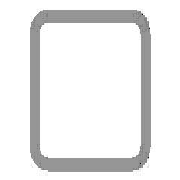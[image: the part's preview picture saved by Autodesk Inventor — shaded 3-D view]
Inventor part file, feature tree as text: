
AUTODESK INVENTOR PART (.ipt)
format: ipt  version: 2025.1 (Build 291241000, 241)  size: 209,920 bytes
history: native  units: mm (DEFAULTED — no unit token found)
features: other x18, sketch x4, extrude x3, plane x1
ambient origin geometry x8: Origin, YZ Plane, XZ Plane, XY Plane, X Axis, Y Axis, Z Axis, Center Point
bodies: Solid1 (feature_tree)
feature tree (26):
  parser-record x1  (decoder bookkeeping rows leaked as tree rows — omitted from the tree; the rows remain in map.json)
  other  "Driven Length"
  other  "Płaszczyzna początkowa"
  other  "Płaszczyzna końcowa"
  extrude  "Bryła"  TaperAngle=0.0deg  [1 undecoded]
  other  "Płaszczyzna konstrukcyjna4"
  other  "Podział1"
  other  "Płaszczyzna konstrukcyjna5"
  other  "Podział2"
  other  "Płaszczyzna konstrukcyjna6"
  other  "Płaszczyzna konstrukcyjna7"
  other  "Płaszczyzna konstrukcyjna8"
  extrude  "Wyciągnięcie proste2"  Depth=4.0mm
  other  "Utwórz kombinację1"
  other  "Płaszczyzna konstrukcyjna9"
  other  "Płaszczyzna konstrukcyjna10"
  other  "Płaszczyzna konstrukcyjna11"
  extrude  "Wyciągnięcie proste3"  Depth=4.0mm
  other  "Utwórz kombinację2"
  sketch  "Sketch3"  dims[d3=1740.0mm d4=0.0mm]
  plane  "Work Plane3"
  sketch  "Sketch4"  dims[d7=4.0mm d10=40.0mm d11=40.0mm d12=3.2mm d13=-20.0mm d14=1720.0mm d15=20.0mm d16=20.0mm d17=90.0deg d18=1740.0mm d19=0.13mm d20=0.0mm d21=0.13mm d22=0.0mm]
  sketch  "Szkic5"
  other  "Bryła2"
  sketch  "Szkic6"
  other  "Bryła3"
note: 1 required parameter value undecoded (feature->parameter linkage not recoverable at this tier; creation-order binding heuristic only, values carry confidence <= 0.55)
